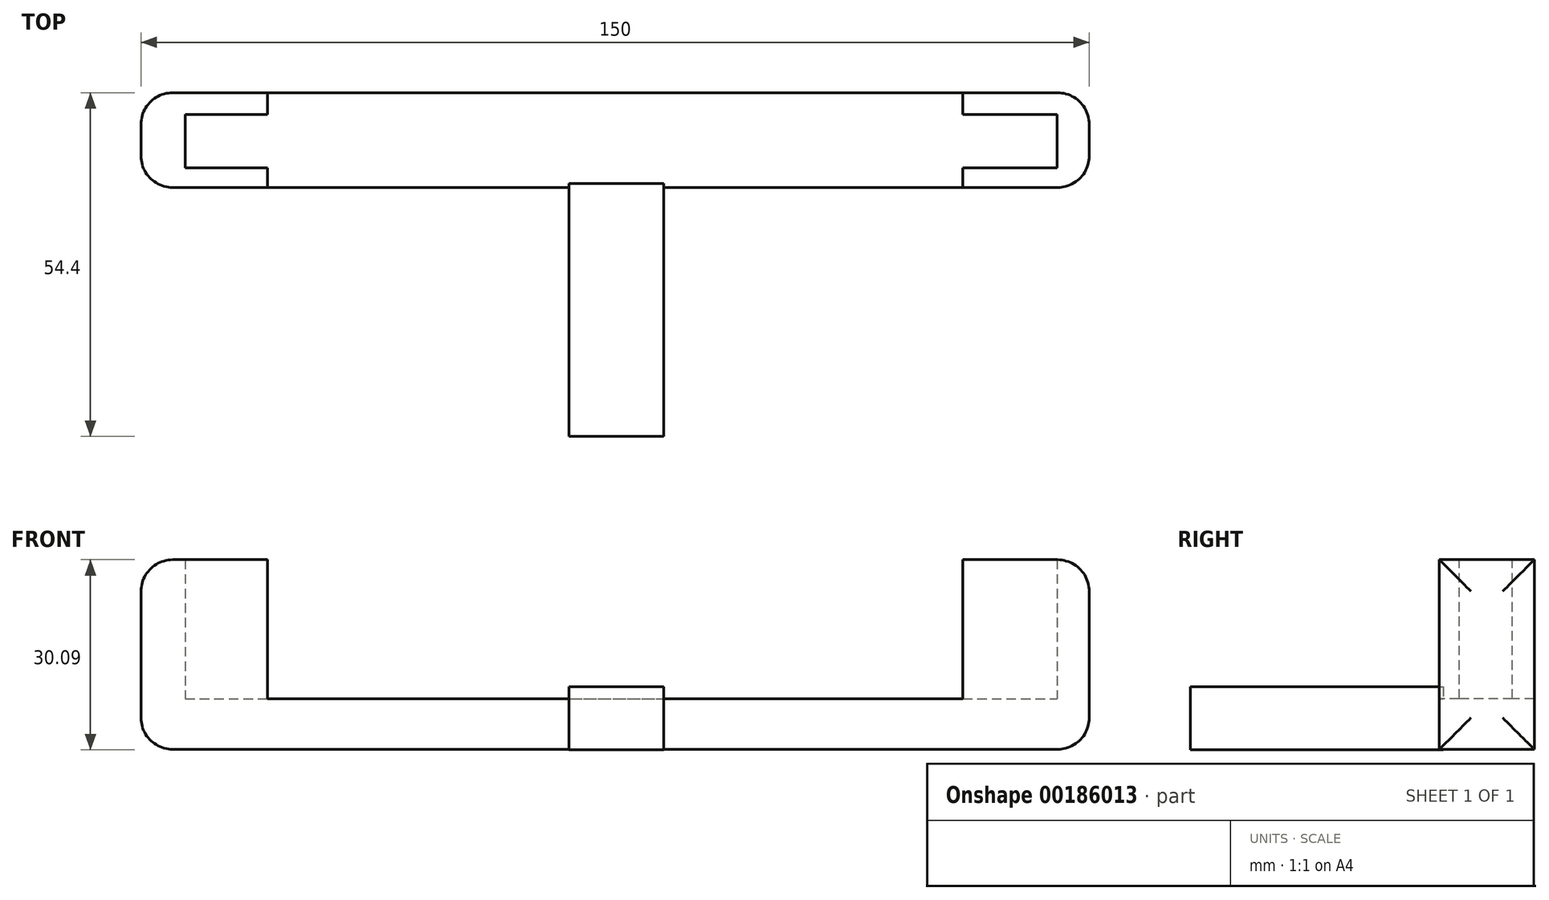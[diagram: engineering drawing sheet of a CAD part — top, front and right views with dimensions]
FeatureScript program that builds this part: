
annotation { "Feature Type Name" : "Feature", "Feature Type Description" : "" }
export const myFeature = defineFeature(function(context is Context, id is Id, definition is map)
    precondition{}
    {
        {
            var Q0;
            Q0=qCreatedBy(makeId("Front.planeOp"),FACE);
            var sketch = newSketch(context, id + "F0", { "sketchPlane" : qUnion([Q0])});
            skLineSegment(sketch, "E0.bottom", {"start": v(0, 19.8) * mm, "end": v(15, 19.8) * mm});
            skLineSegment(sketch, "E0.top", {"start": v(0, 9.8) * mm, "end": v(15, 9.8) * mm});
            skLineSegment(sketch, "E0.left", {"start": v(0, 19.8) * mm, "end": v(0, 9.8) * mm});
            skLineSegment(sketch, "E0.right", {"start": v(15, 19.8) * mm, "end": v(15, 9.8) * mm});
            skSolve(sketch);
        }
        {
            var Q0;
            Q0 = qSketchRegion(id + "F0", true);
            extrude(context, id + "F1", {"entities" : qUnion([Q0]), "depth" : 40 * mm});
        }
        {
            var Q0;
            Q0=makeQuery(id+"F1.opExtrude","SWEPT_BODY",BODY,{"disambiguationData":[OSD([sQuery(id+"F0.wireOp",EDGE,"E0.bottom"),sQuery(id+"F0.wireOp",EDGE,"E0.top"),sQuery(id+"F0.wireOp",EDGE,"E0.left"),sQuery(id+"F0.wireOp",EDGE,"E0.right")])]});
            transform(context, id + "F2", {"entities" : qUnion([Q0]), "transformType" : TransformType.TRANSLATION_3D, "dx" : 0 * mm, "dy" : 0.6 * mm, "dz" : -9.6 * mm, "makeCopy" : false});
        }
        {
            var Q0;
            Q0=makeQuery(id+"F1.opExtrude","SWEPT_BODY",BODY,{"disambiguationData":[OSD([sQuery(id+"F0.wireOp",EDGE,"E0.bottom"),sQuery(id+"F0.wireOp",EDGE,"E0.top"),sQuery(id+"F0.wireOp",EDGE,"E0.left"),sQuery(id+"F0.wireOp",EDGE,"E0.right")])]});
            transform(context, id + "F3", {"entities" : qUnion([Q0]), "transformType" : TransformType.TRANSLATION_3D, "dx" : -7.3 * mm, "dy" : 0 * mm, "dz" : -0.3 * mm, "makeCopy" : false});
        }
        {
            var Q0;
            Q0=qCreatedBy(makeId("Front.planeOp"),FACE);
            var sketch = newSketch(context, id + "F4", { "sketchPlane" : qUnion([Q0])});
            skLineSegment(sketch, "E1", {"start": v(75, 30) * mm, "end": v(75, 0) * mm});
            skLineSegment(sketch, "E2", {"start": v(75, 0) * mm, "end": v(0, 0) * mm});
            skLineSegment(sketch, "E3", {"start": v(0, 0) * mm, "end": v(0, 8) * mm});
            skLineSegment(sketch, "E4", {"start": v(0, 8) * mm, "end": v(55, 8) * mm});
            skLineSegment(sketch, "E5", {"start": v(55, 8) * mm, "end": v(55, 30) * mm});
            skLineSegment(sketch, "E6", {"start": v(55, 30) * mm, "end": v(75, 30) * mm});
            skSolve(sketch);
        }
        {
            var Q0;
            Q0 = qSketchRegion(id + "F4", true);
            extrude(context, id + "F5", {"entities" : qUnion([Q0]), "oppositeDirection" : true, "depth" : 15 * mm});
        }
        {
            var Q0;
            Q0=makeQuery(id+"F5.opExtrude","SWEPT_BODY",BODY,{"disambiguationData":[OSD([sQuery(id+"F4.wireOp",EDGE,"E1"),sQuery(id+"F4.wireOp",EDGE,"E2"),sQuery(id+"F4.wireOp",EDGE,"E3"),sQuery(id+"F4.wireOp",EDGE,"E4"),sQuery(id+"F4.wireOp",EDGE,"E5"),sQuery(id+"F4.wireOp",EDGE,"E6")])]});
            var Q1;
            Q1=qCreatedBy(makeId("Right.planeOp"),FACE);
            mirror(context, id + "F6", {"operationType" : NewBodyOperationType.ADD, "entities" : qUnion([Q0]), "mirrorPlane" : qUnion([Q1])});
        }
        {
            var Q0;
            {var subQ0=makeQuery(id+"F5.opExtrude","SWEPT_FACE",FACE,{"disambiguationData":[OSD([sQuery(id+"F4.wireOp",EDGE,"E4")])]});Q0=makeQuery(id+"F6.boolean.opBoolean","MERGE",FACE,{"derivedFrom":[subQ0,makeQuery(id+"F6.opPattern","COPY",FACE,{"derivedFrom":subQ0,"instanceName":"1"})]});}
            var sketch = newSketch(context, id + "F7", { "sketchPlane" : qUnion([Q0])});
            skLineSegment(sketch, "E7.bottom", {"start": v(-68, 11.55) * mm, "end": v(69.94, 11.55) * mm});
            skLineSegment(sketch, "E7.top", {"start": v(-68, 3.13) * mm, "end": v(69.94, 3.13) * mm});
            skLineSegment(sketch, "E7.left", {"start": v(-68, 11.55) * mm, "end": v(-68, 3.13) * mm});
            skLineSegment(sketch, "E7.right", {"start": v(69.94, 11.55) * mm, "end": v(69.94, 3.13) * mm});
            skSolve(sketch);
        }
        {
            var Q0;
            Q0 = qSketchRegion(id + "F7", true);
            var Q1;
            Q1=makeQuery(id+"F6.opPattern","COPY",FACE,{"derivedFrom":makeQuery(id+"F5.opExtrude","SWEPT_FACE",FACE,{"disambiguationData":[OSD([sQuery(id+"F4.wireOp",EDGE,"E6")])]}),"instanceName":"1"});
            extrude(context, id + "F8", {"entities" : qUnion([Q0]), "operationType" : NewBodyOperationType.REMOVE, "endBound" : BoundingType.UP_TO_SURFACE, "endBoundEntityFace" : qUnion([Q1]), "depth" : 25 * mm});
        }
        {
            var Q0;
            Q0=makeQuery(id+"F1.opExtrude","SWEPT_BODY",BODY,{"disambiguationData":[OSD([sQuery(id+"F0.wireOp",EDGE,"E0.bottom"),sQuery(id+"F0.wireOp",EDGE,"E0.top"),sQuery(id+"F0.wireOp",EDGE,"E0.left"),sQuery(id+"F0.wireOp",EDGE,"E0.right")])]});
            var Q1;
            Q1=makeQuery(id+"F1.opExtrude","CAP_FACE",FACE,{"disambiguationData":[OSD([sQuery(id+"F0.wireOp",EDGE,"E0.bottom"),sQuery(id+"F0.wireOp",EDGE,"E0.top"),sQuery(id+"F0.wireOp",EDGE,"E0.left"),sQuery(id+"F0.wireOp",EDGE,"E0.right")])],"isStart":false});
            transform(context, id + "F9", {"entities" : qUnion([Q0]), "transformType" : TransformType.TRANSLATION_DISTANCE, "transformDirection" : qUnion([Q1]), "distance" : 1 * mm, "oppositeDirection" : true, "makeCopy" : false});
        }
        {
            var Q0;
            {var subQ0=makeQuery(id+"F5.opExtrude","CAP_FACE",FACE,{"disambiguationData":[OSD([sQuery(id+"F4.wireOp",EDGE,"E1"),sQuery(id+"F4.wireOp",EDGE,"E2"),sQuery(id+"F4.wireOp",EDGE,"E3"),sQuery(id+"F4.wireOp",EDGE,"E4"),sQuery(id+"F4.wireOp",EDGE,"E5"),sQuery(id+"F4.wireOp",EDGE,"E6")])],"isStart":true});Q0=makeQuery(id+"F6.boolean.opBoolean","MERGE",FACE,{"derivedFrom":[subQ0,makeQuery(id+"F6.opPattern","COPY",FACE,{"derivedFrom":subQ0,"instanceName":"1"})]});}
            var sketch = newSketch(context, id + "F10", { "sketchPlane" : qUnion([Q0])});
            skLineSegment(sketch, "E8.bottom", {"start": v(-16.02, 8) * mm, "end": v(19.2, 8) * mm});
            skLineSegment(sketch, "E8.top", {"start": v(-16.02, 0) * mm, "end": v(19.2, 0) * mm});
            skLineSegment(sketch, "E8.left", {"start": v(-16.02, 8) * mm, "end": v(-16.02, 0) * mm});
            skLineSegment(sketch, "E8.right", {"start": v(19.2, 8) * mm, "end": v(19.2, 0) * mm});
            skSolve(sketch);
        }
        {
            var Q0;
            Q0=makeQuery(id+"F6.opPattern","COPY",EDGE,{"derivedFrom":makeQuery(id+"F5.opExtrude","CAP_EDGE",EDGE,{"disambiguationData":[OSD([sQuery(id+"F4.wireOp",EDGE,"E1")])],"isStart":false}),"instanceName":"1"});
            var Q1;
            Q1=makeQuery(id+"F6.opPattern","COPY",FACE,{"derivedFrom":makeQuery(id+"F5.opExtrude","SWEPT_FACE",FACE,{"disambiguationData":[OSD([sQuery(id+"F4.wireOp",EDGE,"E1")])]}),"instanceName":"1"});
            var Q2;
            Q2=makeQuery(id+"F5.opExtrude","SWEPT_FACE",FACE,{"disambiguationData":[OSD([sQuery(id+"F4.wireOp",EDGE,"E1")])]});
            fillet(context, id + "F11", {"entities" : qUnion([Q0, Q1, Q2]), "radius" : 5 * mm, "tangentPropagation" : true, "allowEdgeOverflow" : false});
        }
    });
